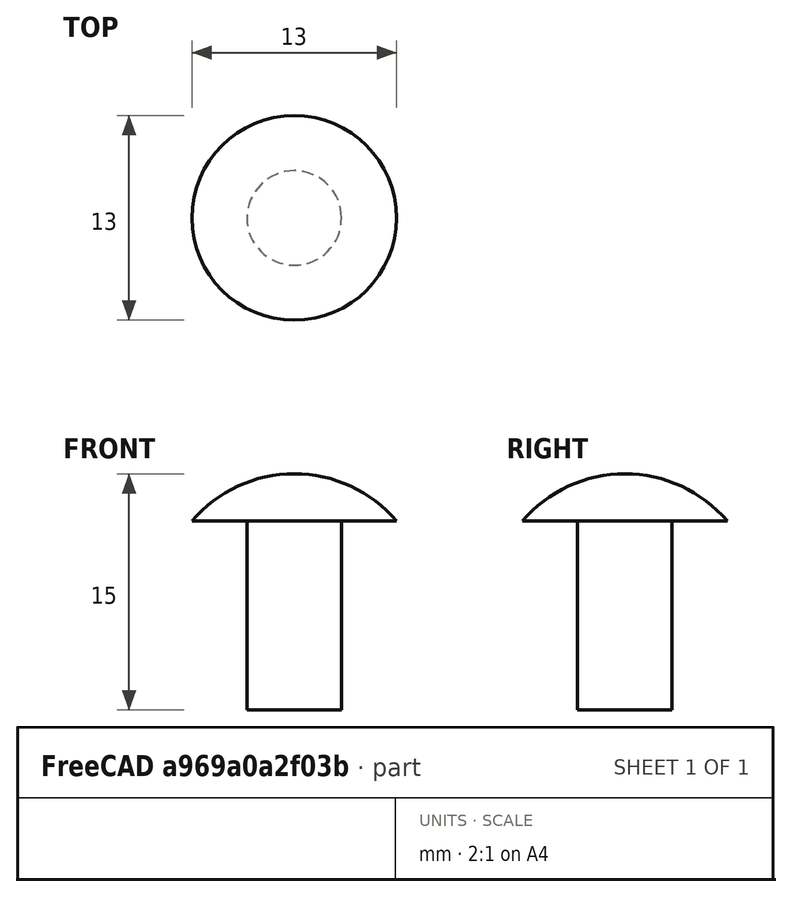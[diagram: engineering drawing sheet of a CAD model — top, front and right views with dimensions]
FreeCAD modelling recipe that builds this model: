
FCSTD DOCUMENT  (FreeCAD 0.18R14555 (Git shallow))
Label: m6-12
License: All rights reserved
LicenseURL: http://en.wikipedia.org/wiki/All_rights_reserved
objects: Sketcher::SketchObject×1, PartDesign::Revolution×1, PartDesign::Body×1
note: 4 computed .brp shape members not serialized (recipe doc carries the construction recipe); baked Part::Feature solids carry a one-line shape summary decoded from their .brp

FEATURE [Sketcher::SketchObject] Sketch
  MapMode = 5
  Placement = pos=(0,0,0) rot=(1,0,0;1.5708rad)
  Support = -> [XZ_Plane]
  sketch-geometry (5):
    g0: LineSegment StartX=0 StartY=15 StartZ=0 EndX=0 EndY=0 EndZ=0
    g1: LineSegment StartX=0 StartY=0 StartZ=0 EndX=3 EndY=0 EndZ=0
    g2: ArcOfCircle CenterX=0 CenterY=6.45833 CenterZ=0 NormalX=0 NormalY=0 NormalZ=1 AngleXU=0 Radius=8.54167 StartAngle=0.705981 EndAngle=1.5708
    g3: LineSegment StartX=3 StartY=0 StartZ=0 EndX=3 EndY=12 EndZ=0
    g4: LineSegment StartX=3 StartY=12 StartZ=0 EndX=6.5 EndY=12 EndZ=0
  constraints (15):
    c: Vertical(g0)
    c: Coincident(g0,g1)
    c: Horizontal(g1)
    c: Coincident(g2,g0)
    c: Coincident(g1,g3)
    c: Vertical(g3)
    c: Coincident(g3,g4)
    c: Coincident(g4,g2)
    c: Horizontal(g4)
    c: Coincident(g0,g-1)
    c: DistanceX(g1,g1) = 3
    c: DistanceX(g0,g2) = 6.5
    c: DistanceY(g3,g3) = 12
    c: DistanceY(g3,g0) = 3
    c: Perpendicular(g2,g0)
FEATURE [PartDesign::Revolution] Revolution
  Angle = 360
  Axis = (0,2e-16,1)
  Base = (0,0,0)
  Placement = pos=(0,0,0) rot=(1,0,0;1.5708rad)
  Profile = -> Sketch
  ReferenceAxis = -> Sketch [V_Axis]
  Reversed = true
FEATURE [PartDesign::Body] Body
  Group = -> [Sketch,Revolution]
  Origin = -> Origin
  Tip = -> Revolution
